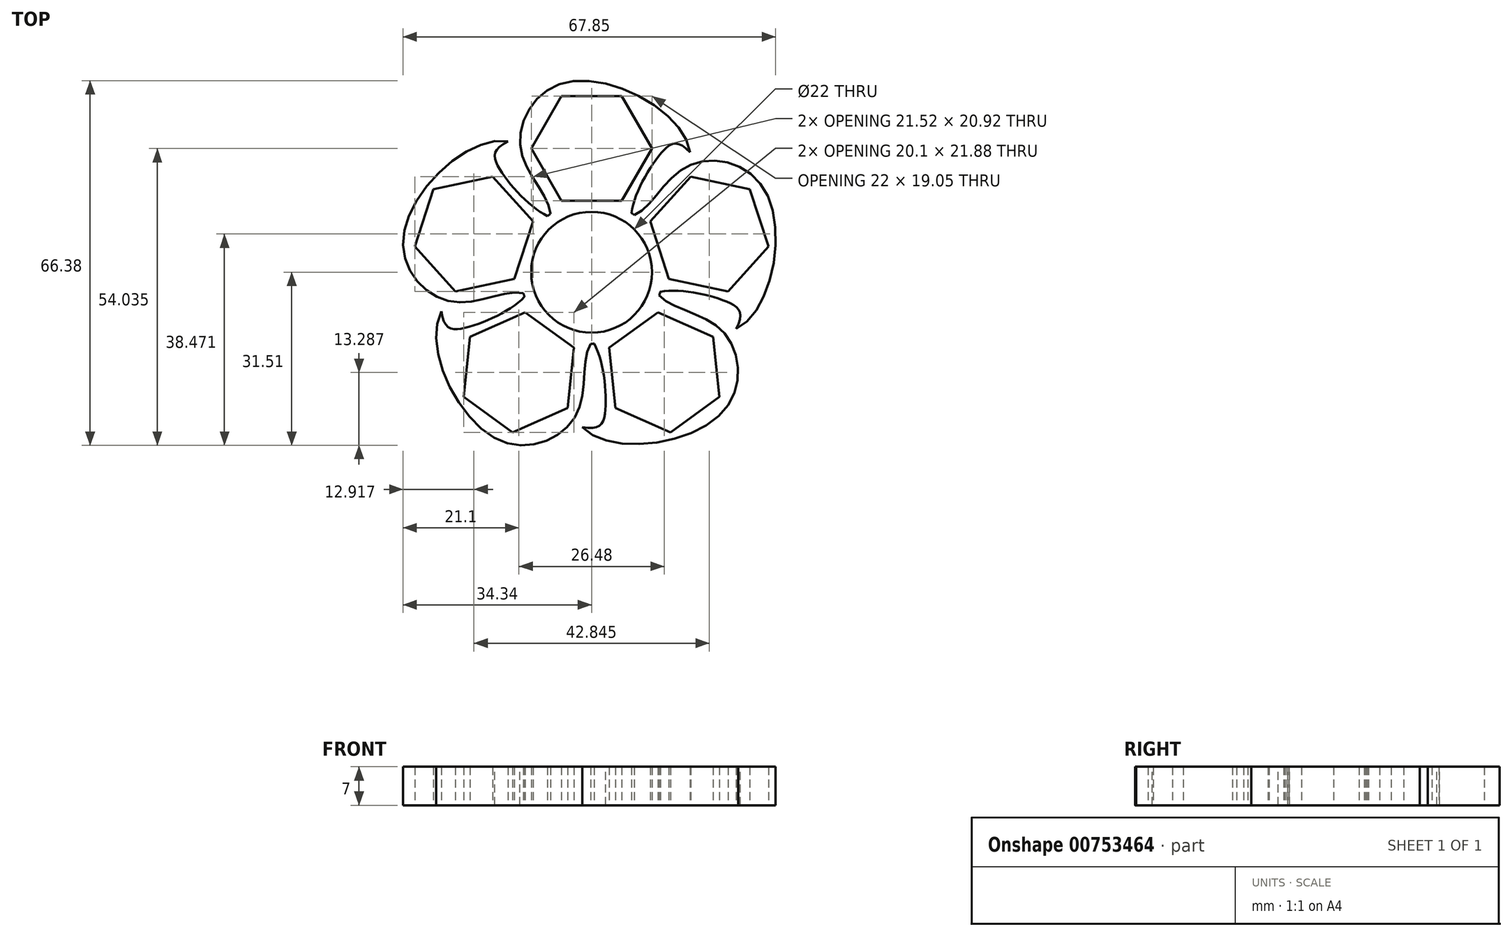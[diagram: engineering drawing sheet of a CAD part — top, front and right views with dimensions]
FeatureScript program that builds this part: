
annotation { "Feature Type Name" : "Feature", "Feature Type Description" : "" }
export const myFeature = defineFeature(function(context is Context, id is Id, definition is map)
    precondition{}
    {
        {
            var Q0;
            Q0=qCreatedBy(makeId("Top.planeOp"),FACE);
            var sketch = newSketch(context, id + "F0", { "sketchPlane" : qUnion([Q0])});
            skPoint(sketch, "E0", {"position": v(0, 0) * mm});
            skCircle(sketch, "E1", {"center": v(0, 0) * mm, "radius": 13 * mm});
            skCircle(sketch, "E2", {"center": v(0, 0) * mm, "radius": 11 * mm});
            skCircle(sketch, "E3", {"center": v(0, 22.52) * mm, "radius": 9.53 * mm});
            skCircle(sketch, "E4.cCircle", {"center": v(0, 22.52) * mm, "radius": 9.52 * mm, "construction": true});
            skLineSegment(sketch, "E4.0", {"start": v(5.5, 13) * mm, "end": v(-5.5, 13) * mm});
            skLineSegment(sketch, "E4.1", {"start": v(-5.5, 13) * mm, "end": v(-11, 22.52) * mm});
            skLineSegment(sketch, "E4.2", {"start": v(-11, 22.52) * mm, "end": v(-5.5, 32.05) * mm});
            skLineSegment(sketch, "E4.3", {"start": v(-5.5, 32.05) * mm, "end": v(5.5, 32.05) * mm});
            skLineSegment(sketch, "E4.4", {"start": v(5.5, 32.05) * mm, "end": v(11, 22.53) * mm});
            skLineSegment(sketch, "E4.5", {"start": v(11, 22.52) * mm, "end": v(5.5, 13) * mm});
            skPoint(sketch, "E4.0.midPoint", {"position": v(0, 13) * mm});
            skFitSpline(sketch, "E5", {"points": [v(-7.5, 10.62) * mm, v(-12.92, 22.38) * mm, v(-3.98, 34.7) * mm, v(17.93, 21.81) * mm], "startDerivative": vector(-2.02, 36.08) * mm, "endDerivative": vector(6.92, -53.27) * mm});
            skFitSpline(sketch, "E6", {"points": [v(17.93, 21.81) * mm, v(12.6, 21.64) * mm, v(7.25, 10.79) * mm], "startDerivative": vector(-17.93, 19.52) * mm, "endDerivative": vector(-2.13, -16.78) * mm});
            skSolve(sketch);
        }
        {
            var Q0;
            {var subQ17=sQuery(id+"F0.wireOp",EDGE,"E5");Q0=makeQuery(id+"F0.imprint","IMPRINT",FACE,{"disambiguationData":[TD([[makeQuery(id+"F0.imprint","IMPRINT",EDGE,{"derivedFrom":subQ17}),-1.0]])]});}
            var Q1;
            Q1=makeQuery(id+"F0.imprint","IMPRINT",FACE,{"disambiguationData":[TD([[makeQuery(id+"F0.imprint","IMPRINT",EDGE,{"derivedFrom":sQuery(id+"F0.wireOp",EDGE,"E2")}),-1.0]])]});
            extrude(context, id + "F1", {"entities" : qUnion([Q0, Q1]), "depth" : 7 * mm, "offsetDistance" : 25 * mm});
        }
        {
            var Q0;
            Q0=makeQuery(id+"F1.opExtrude","SWEPT_BODY",BODY,{"disambiguationData":[OSD([sQuery(id+"F0.wireOp",EDGE,"E1"),sQuery(id+"F0.wireOp",EDGE,"E2"),sQuery(id+"F0.wireOp",EDGE,"E4.0"),sQuery(id+"F0.wireOp",EDGE,"E4.1"),sQuery(id+"F0.wireOp",EDGE,"E4.2"),sQuery(id+"F0.wireOp",EDGE,"E4.3"),sQuery(id+"F0.wireOp",EDGE,"E4.4"),sQuery(id+"F0.wireOp",EDGE,"E4.5"),sQuery(id+"F0.wireOp",EDGE,"E5"),sQuery(id+"F0.wireOp",EDGE,"E6")])]});
            var Q1;
            Q1=makeQuery(id+"F1.opExtrude","CAP_EDGE",EDGE,{"disambiguationData":[OSD([sQuery(id+"F0.wireOp",EDGE,"E2")])],"isStart":false});
            circularPattern(context, id + "F2", {"operationType" : NewBodyOperationType.ADD, "entities" : qUnion([Q0]), "axis" : qUnion([Q1]), "angle" : 360 * degree, "instanceCount" : 5, "equalSpace" : true});
        }
    });
